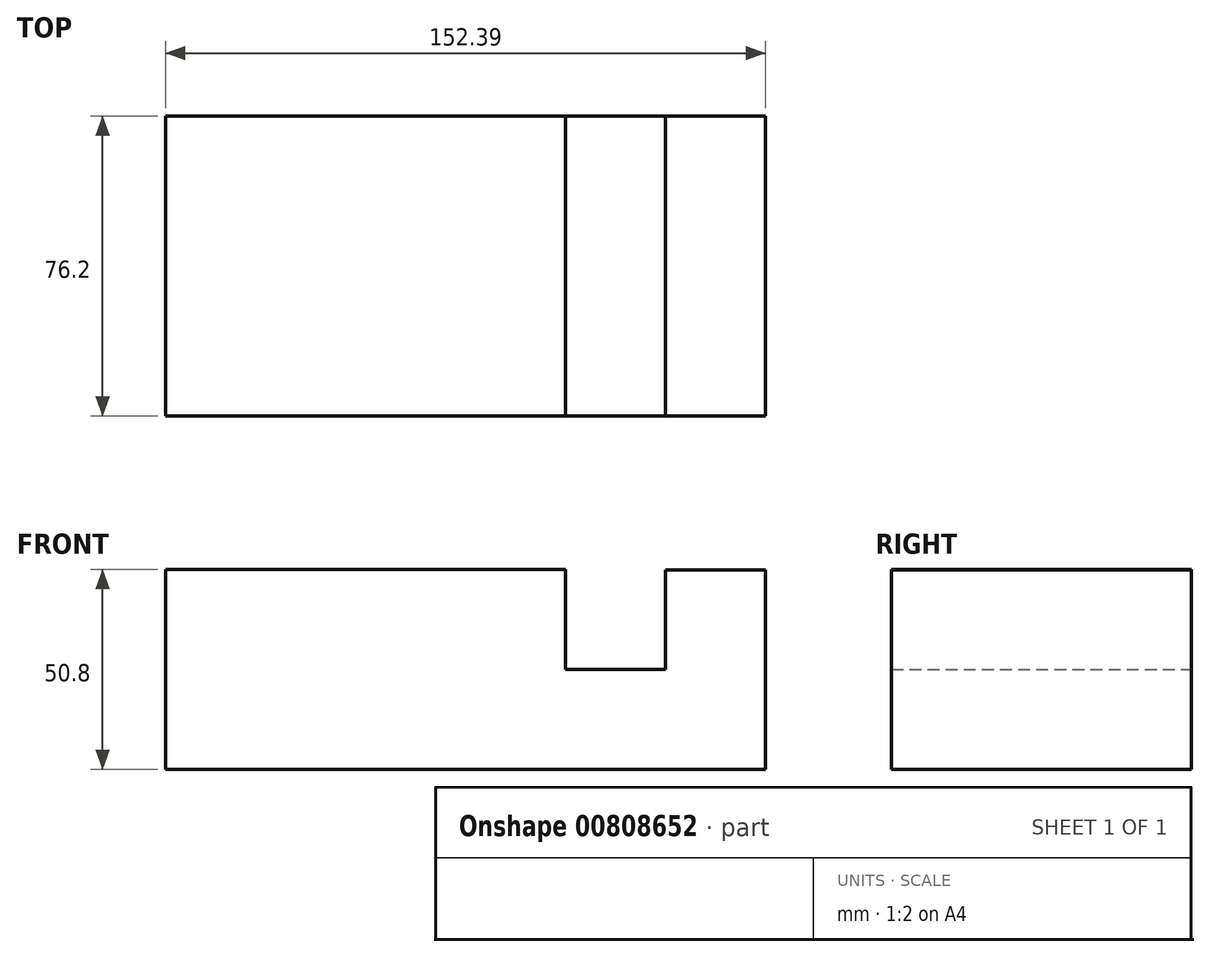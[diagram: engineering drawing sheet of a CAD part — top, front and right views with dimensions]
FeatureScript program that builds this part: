
annotation { "Feature Type Name" : "Feature", "Feature Type Description" : "" }
export const myFeature = defineFeature(function(context is Context, id is Id, definition is map)
    precondition{}
    {
        {
            var Q0;
            Q0=qCreatedBy(makeId("Front.planeOp"),FACE);
            var sketch = newSketch(context, id + "F0", { "sketchPlane" : qUnion([Q0])});
            skLineSegment(sketch, "E0", {"start": v(0, 0) * mm, "end": v(0, 50.8) * mm});
            skLineSegment(sketch, "E1", {"start": v(0, 50.8) * mm, "end": v(101.6, 50.8) * mm});
            skLineSegment(sketch, "E2", {"start": v(101.6, 50.8) * mm, "end": v(101.6, 25.4) * mm});
            skLineSegment(sketch, "E3", {"start": v(101.6, 25.4) * mm, "end": v(127, 25.4) * mm});
            skLineSegment(sketch, "E4", {"start": v(127, 25.4) * mm, "end": v(127, 50.8) * mm});
            skLineSegment(sketch, "E5", {"start": v(127, 50.7) * mm, "end": v(152.4, 50.7) * mm});
            skLineSegment(sketch, "E6", {"start": v(152.4, 50.7) * mm, "end": v(152.4, 25.4) * mm});
            skLineSegment(sketch, "E7", {"start": v(152.4, 25.4) * mm, "end": v(152.4, 0) * mm});
            skLineSegment(sketch, "E8", {"start": v(152.4, 0) * mm, "end": v(0, 0) * mm});
            skSolve(sketch);
        }
        {
            var Q0;
            Q0 = qSketchRegion(id + "F0", true);
            extrude(context, id + "F1", {"entities" : qUnion([Q0]), "depth" : 76.2 * mm, "offsetDistance" : 25.4 * mm});
        }
    });
